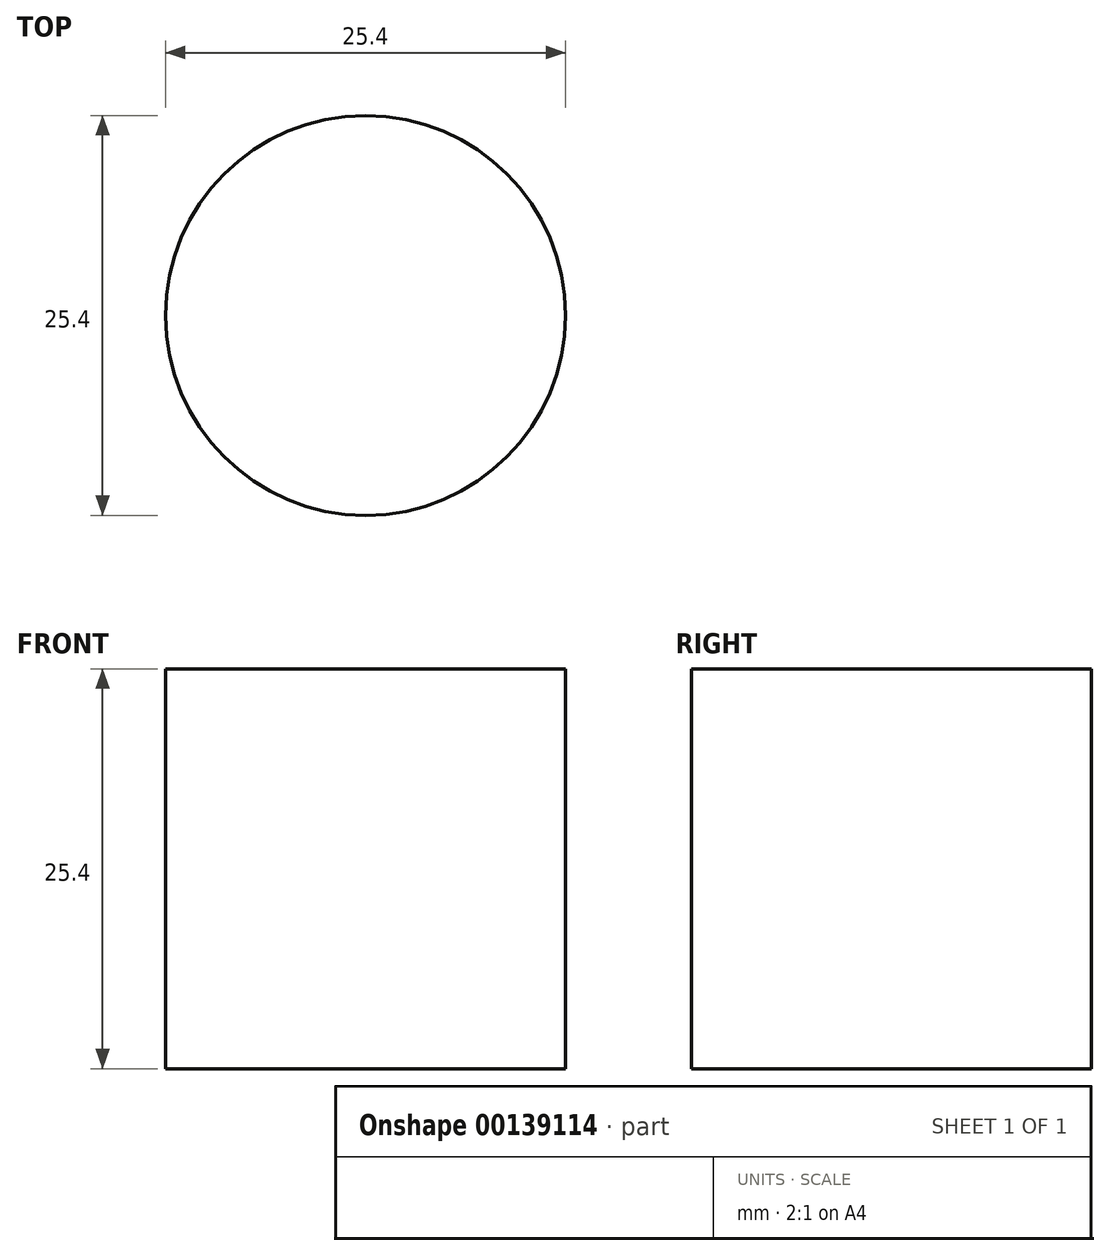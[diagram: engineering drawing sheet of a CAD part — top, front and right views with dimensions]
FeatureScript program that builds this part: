
annotation { "Feature Type Name" : "Feature", "Feature Type Description" : "" }
export const myFeature = defineFeature(function(context is Context, id is Id, definition is map)
    precondition{}
    {
        {
            var Q0;
            Q0=qCreatedBy(makeId("Top.planeOp"),FACE);
            var sketch = newSketch(context, id + "F0", { "sketchPlane" : qUnion([Q0])});
            skCircle(sketch, "E0", {"center": v(0, -1.25) * mm, "radius": 12.7 * mm});
            skSolve(sketch);
        }
        {
            var Q0;
            Q0 = qSketchRegion(id + "F0", true);
            extrude(context, id + "F1", {"entities" : qUnion([Q0]), "depth" : 25.4 * mm});
        }
    });
